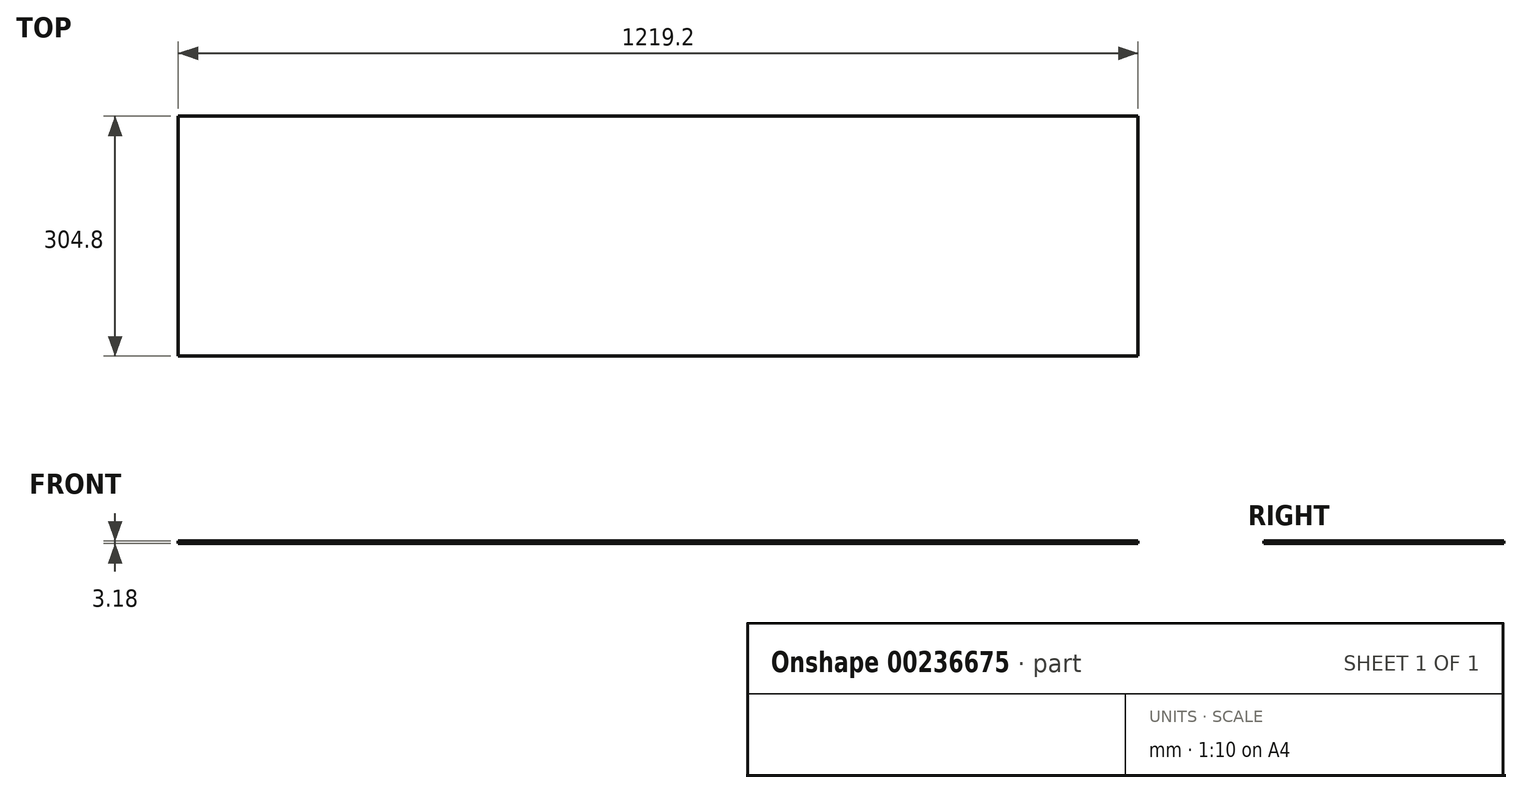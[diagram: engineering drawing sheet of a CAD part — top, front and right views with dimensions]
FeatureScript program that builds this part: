
annotation { "Feature Type Name" : "Feature", "Feature Type Description" : "" }
export const myFeature = defineFeature(function(context is Context, id is Id, definition is map)
    precondition{}
    {
        {
            var Q0;
            Q0=qCreatedBy(makeId("Top.planeOp"),FACE);
            var sketch = newSketch(context, id + "F0", { "sketchPlane" : qUnion([Q0])});
            skLineSegment(sketch, "E0.bottom", {"start": v(609.6, -152.4) * mm, "end": v(-609.6, -152.4) * mm});
            skLineSegment(sketch, "E0.top", {"start": v(609.6, 152.4) * mm, "end": v(-609.6, 152.4) * mm});
            skLineSegment(sketch, "E0.left", {"start": v(609.6, -152.4) * mm, "end": v(609.6, 152.4) * mm});
            skLineSegment(sketch, "E0.right", {"start": v(-609.6, -152.4) * mm, "end": v(-609.6, 152.4) * mm});
            skPoint(sketch, "E0.middle", {"position": v(0, 0) * mm});
            skSolve(sketch);
        }
        {
            var Q0;
            Q0 = qSketchRegion(id + "F0", true);
            extrude(context, id + "F1", {"entities" : qUnion([Q0]), "endBound" : BoundingType.SYMMETRIC, "depth" : 3.17 * mm});
        }
    });
